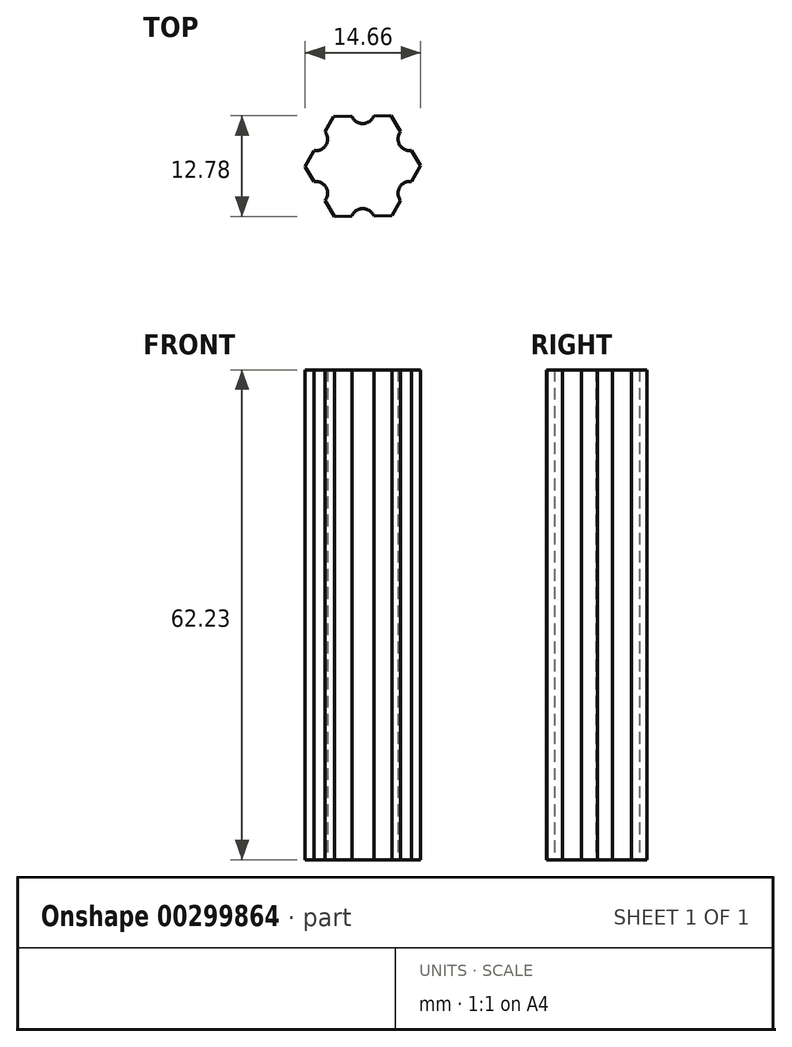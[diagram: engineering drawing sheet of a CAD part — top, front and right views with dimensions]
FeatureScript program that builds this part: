
annotation { "Feature Type Name" : "Feature", "Feature Type Description" : "" }
export const myFeature = defineFeature(function(context is Context, id is Id, definition is map)
    precondition{}
    {
        {
            var Q0;
            Q0=qCreatedBy(makeId("Top.planeOp"),FACE);
            var sketch = newSketch(context, id + "F0", { "sketchPlane" : qUnion([Q0])});
            skCircle(sketch, "E0.cCircle", {"center": v(0, 0) * mm, "radius": 6.35 * mm, "construction": true});
            skLineSegment(sketch, "E0.0", {"start": v(-3.6, -6.4) * mm, "end": v(-7.33, -0.08) * mm});
            skLineSegment(sketch, "E0.1", {"start": v(-7.33, -0.08) * mm, "end": v(-3.74, 6.3) * mm});
            skLineSegment(sketch, "E0.2", {"start": v(-3.74, 6.3) * mm, "end": v(3.6, 6.4) * mm});
            skLineSegment(sketch, "E0.3", {"start": v(3.6, 6.4) * mm, "end": v(7.33, 0.08) * mm});
            skLineSegment(sketch, "E0.4", {"start": v(7.33, 0.08) * mm, "end": v(3.74, -6.3) * mm});
            skLineSegment(sketch, "E0.5", {"start": v(3.74, -6.3) * mm, "end": v(-3.6, -6.4) * mm});
            skPoint(sketch, "E0.0.midPoint", {"position": v(-5.46, -3.24) * mm});
            skSolve(sketch);
        }
        {
            var Q0;
            Q0=makeQuery(id+"F0.imprint","IMPRINT",FACE,{"disambiguationData":[TD([[makeQuery(id+"F0.imprint","IMPRINT",EDGE,{"derivedFrom":sQuery(id+"F0.wireOp",EDGE,"E0.0")}),-1.0]])]});
            extrude(context, id + "F1", {"entities" : qUnion([Q0]), "depth" : 62.23 * mm});
        }
        {
            var Q0;
            Q0=makeQuery(id+"F1.opExtrude","CAP_FACE",FACE,{"disambiguationData":[OSD([sQuery(id+"F0.wireOp",EDGE,"E0.0"),sQuery(id+"F0.wireOp",EDGE,"E0.1"),sQuery(id+"F0.wireOp",EDGE,"E0.2"),sQuery(id+"F0.wireOp",EDGE,"E0.3"),sQuery(id+"F0.wireOp",EDGE,"E0.4"),sQuery(id+"F0.wireOp",EDGE,"E0.5")])],"isStart":true});
            var sketch = newSketch(context, id + "F2", { "sketchPlane" : qUnion([Q0])});
            skArc(sketch, "E1", {"start": v(-1.4, 6.37) * mm, "mid": v(-0.01, 5.4) * mm, "end": v(1.4, 6.34) * mm});
            skArc(sketch, "E2.1.0", {"start": v(-6.21, 1.98) * mm, "mid": v(-4.68, 2.69) * mm, "end": v(-4.8, 4.37) * mm});
            skArc(sketch, "E2.2.0", {"start": v(-4.82, -4.4) * mm, "mid": v(-4.67, -2.7) * mm, "end": v(-6.18, -1.96) * mm});
            skArc(sketch, "E2.3.0", {"start": v(1.4, -6.37) * mm, "mid": v(0.01, -5.4) * mm, "end": v(-1.4, -6.34) * mm});
            skArc(sketch, "E2.4.0", {"start": v(6.21, -1.98) * mm, "mid": v(4.68, -2.69) * mm, "end": v(4.8, -4.37) * mm});
            skArc(sketch, "E2.5.0", {"start": v(4.82, 4.4) * mm, "mid": v(4.67, 2.7) * mm, "end": v(6.18, 1.96) * mm});
            skPoint(sketch, "E2.center", {"position": v(0, 0) * mm});
            skSolve(sketch);
        }
        {
            var Q0;
            {var subQ0=sQuery(id+"F2.wireOp",EDGE,"E2.1.0");Q0=makeQuery(id+"F2.imprint","IMPRINT",FACE,{"disambiguationData":[TD([[makeQuery(id+"F2.imprint","IMPRINT",EDGE,{"derivedFrom":subQ0}),1.0]])]});}
            var Q1;
            {var subQ0=sQuery(id+"F2.wireOp",EDGE,"E1");Q1=makeQuery(id+"F2.imprint","IMPRINT",FACE,{"disambiguationData":[TD([[makeQuery(id+"F2.imprint","IMPRINT",EDGE,{"derivedFrom":subQ0}),1.0]])]});}
            var Q2;
            {var subQ0=sQuery(id+"F2.wireOp",EDGE,"E2.5.0");Q2=makeQuery(id+"F2.imprint","IMPRINT",FACE,{"disambiguationData":[TD([[makeQuery(id+"F2.imprint","IMPRINT",EDGE,{"derivedFrom":subQ0}),1.0]])]});}
            var Q3;
            {var subQ0=sQuery(id+"F2.wireOp",EDGE,"E2.4.0");Q3=makeQuery(id+"F2.imprint","IMPRINT",FACE,{"disambiguationData":[TD([[makeQuery(id+"F2.imprint","IMPRINT",EDGE,{"derivedFrom":subQ0}),1.0]])]});}
            var Q4;
            {var subQ0=sQuery(id+"F2.wireOp",EDGE,"E2.3.0");Q4=makeQuery(id+"F2.imprint","IMPRINT",FACE,{"disambiguationData":[TD([[makeQuery(id+"F2.imprint","IMPRINT",EDGE,{"derivedFrom":subQ0}),1.0]])]});}
            var Q5;
            {var subQ0=sQuery(id+"F2.wireOp",EDGE,"E2.2.0");Q5=makeQuery(id+"F2.imprint","IMPRINT",FACE,{"disambiguationData":[TD([[makeQuery(id+"F2.imprint","IMPRINT",EDGE,{"derivedFrom":subQ0}),1.0]])]});}
            var Q6;
            Q6=makeQuery(id+"F1.opExtrude","CAP_FACE",FACE,{"disambiguationData":[OSD([sQuery(id+"F0.wireOp",EDGE,"E0.0"),sQuery(id+"F0.wireOp",EDGE,"E0.1"),sQuery(id+"F0.wireOp",EDGE,"E0.2"),sQuery(id+"F0.wireOp",EDGE,"E0.3"),sQuery(id+"F0.wireOp",EDGE,"E0.4"),sQuery(id+"F0.wireOp",EDGE,"E0.5")])],"isStart":false});
            extrude(context, id + "F3", {"entities" : qUnion([Q0, Q1, Q2, Q3, Q4, Q5]), "operationType" : NewBodyOperationType.REMOVE, "endBound" : BoundingType.UP_TO_SURFACE, "oppositeDirection" : true, "endBoundEntityFace" : qUnion([Q6]), "depth" : 25.4 * mm});
        }
        {
            var Q0;
            Q0=makeQuery(id+"F1.opExtrude","CAP_FACE",FACE,{"disambiguationData":[OSD([sQuery(id+"F0.wireOp",EDGE,"E0.0"),sQuery(id+"F0.wireOp",EDGE,"E0.1"),sQuery(id+"F0.wireOp",EDGE,"E0.2"),sQuery(id+"F0.wireOp",EDGE,"E0.3"),sQuery(id+"F0.wireOp",EDGE,"E0.4"),sQuery(id+"F0.wireOp",EDGE,"E0.5")])],"isStart":false});
            extrude(context, id + "F4", {"entities" : qUnion([Q0]), "operationType" : NewBodyOperationType.ADD, "depth" : 10.8 * mm});
        }
        {
            var Q0;
            Q0=makeQuery(id+"F4.opExtrude","CAP_FACE",FACE,{"disambiguationData":[OSD([sQuery(id+"F0.wireOp",EDGE,"E0.0"),sQuery(id+"F0.wireOp",EDGE,"E0.1"),sQuery(id+"F0.wireOp",EDGE,"E0.2"),sQuery(id+"F0.wireOp",EDGE,"E0.3"),sQuery(id+"F0.wireOp",EDGE,"E0.4"),sQuery(id+"F0.wireOp",EDGE,"E0.5")])],"isStart":false});
            extrude(context, id + "F5", {"entities" : qUnion([Q0]), "operationType" : NewBodyOperationType.REMOVE, "oppositeDirection" : true, "depth" : 10.8 * mm});
        }
    });
